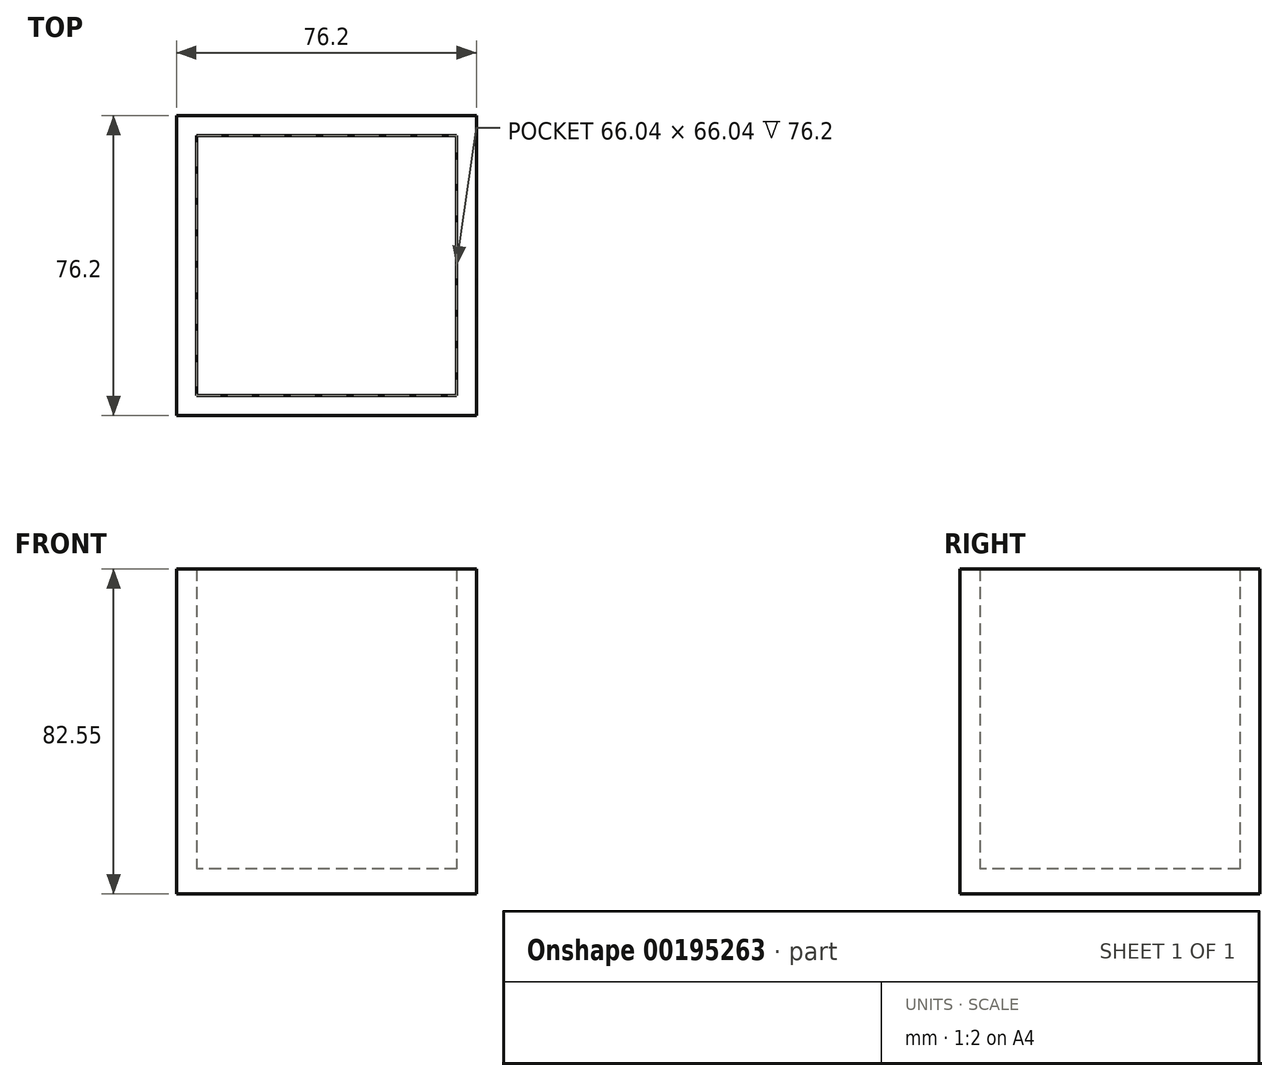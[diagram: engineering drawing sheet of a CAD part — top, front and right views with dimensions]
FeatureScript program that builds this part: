
annotation { "Feature Type Name" : "Feature", "Feature Type Description" : "" }
export const myFeature = defineFeature(function(context is Context, id is Id, definition is map)
    precondition{}
    {
        {
            var Q0;
            Q0=qCreatedBy(makeId("Top.planeOp"),FACE);
            var sketch = newSketch(context, id + "F0", { "sketchPlane" : qUnion([Q0])});
            skLineSegment(sketch, "E0.bottom", {"start": v(38.1, 38.1) * mm, "end": v(-38.1, 38.1) * mm});
            skLineSegment(sketch, "E0.top", {"start": v(38.1, -38.1) * mm, "end": v(-38.1, -38.1) * mm});
            skLineSegment(sketch, "E0.left", {"start": v(38.1, 38.1) * mm, "end": v(38.1, -38.1) * mm});
            skLineSegment(sketch, "E0.right", {"start": v(-38.1, 38.1) * mm, "end": v(-38.1, -38.1) * mm});
            skPoint(sketch, "E0.middle", {"position": v(0, 0) * mm});
            skLineSegment(sketch, "E1.0", {"start": v(33.02, -33.02) * mm, "end": v(-33.02, -33.02) * mm});
            skLineSegment(sketch, "E1.1", {"start": v(33.02, 33.02) * mm, "end": v(33.02, -33.02) * mm});
            skLineSegment(sketch, "E1.2", {"start": v(33.02, 33.02) * mm, "end": v(-33.02, 33.02) * mm});
            skLineSegment(sketch, "E1.3", {"start": v(-33.02, 33.02) * mm, "end": v(-33.02, -33.02) * mm});
            skSolve(sketch);
        }
        {
            var Q0;
            Q0=makeQuery(id+"F0.imprint","IMPRINT",FACE,{"disambiguationData":[TD([[makeQuery(id+"F0.imprint","IMPRINT",EDGE,{"derivedFrom":sQuery(id+"F0.wireOp",EDGE,"E1.0")}),-1.0]])]});
            var Q1;
            Q1=makeQuery(id+"F0.imprint","IMPRINT",FACE,{"disambiguationData":[TD([[makeQuery(id+"F0.imprint","IMPRINT",EDGE,{"derivedFrom":sQuery(id+"F0.wireOp",EDGE,"E0.bottom")}),1.0]])]});
            extrude(context, id + "F1", {"entities" : qUnion([Q0, Q1]), "oppositeDirection" : true, "depth" : 6.35 * mm});
        }
        {
            var Q0;
            Q0 = qSketchRegion(id + "F0", true);
            extrude(context, id + "F2", {"entities" : qUnion([Q0]), "operationType" : NewBodyOperationType.ADD, "depth" : 76.2 * mm});
        }
    });
